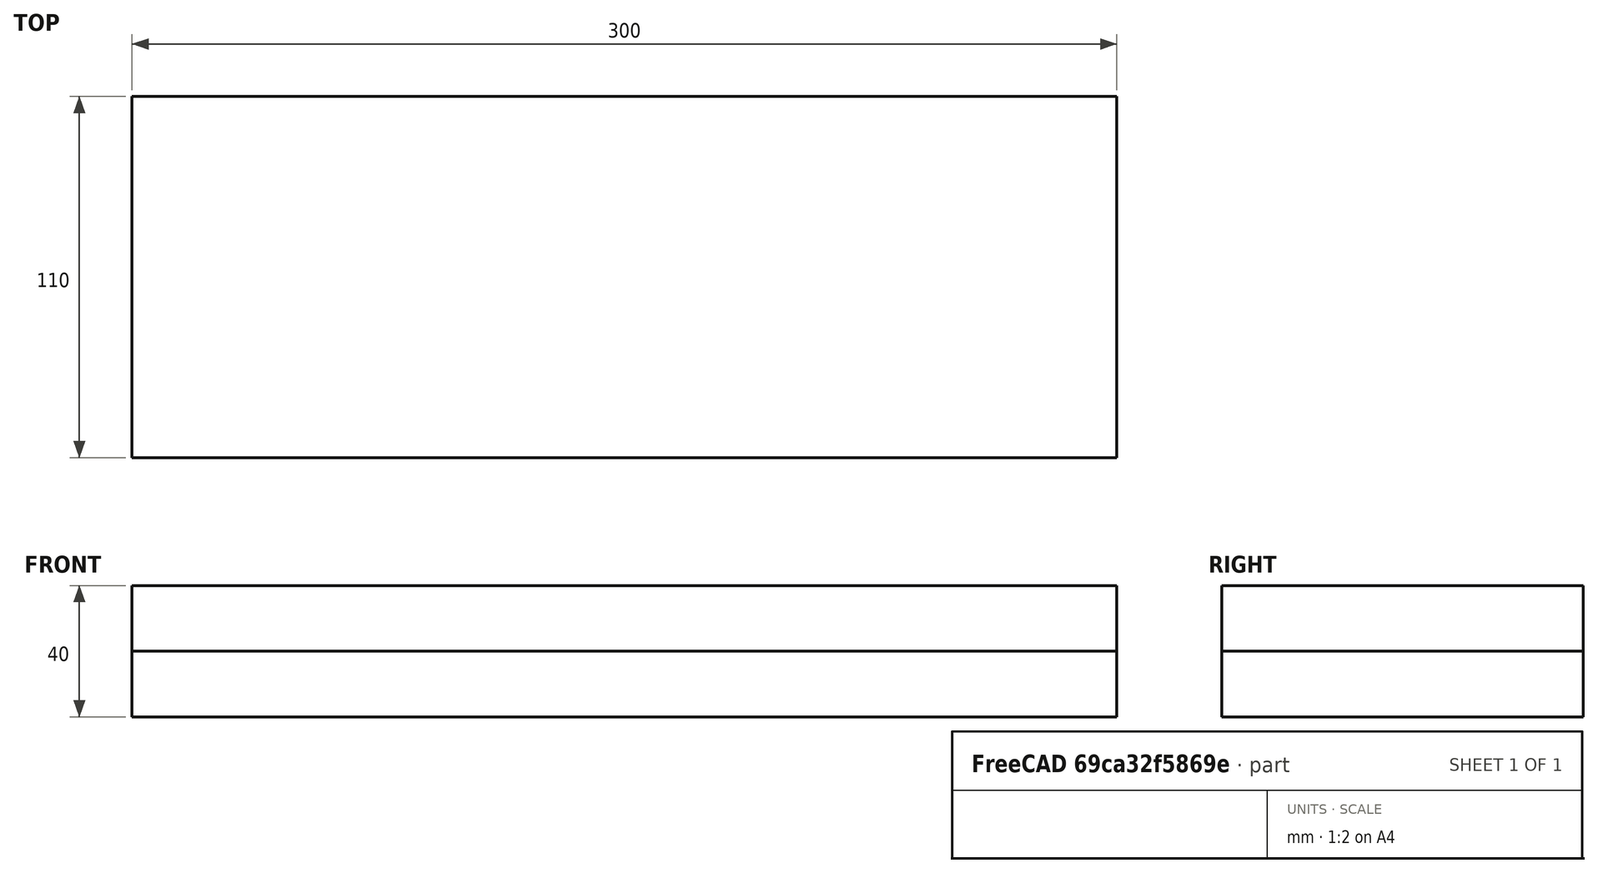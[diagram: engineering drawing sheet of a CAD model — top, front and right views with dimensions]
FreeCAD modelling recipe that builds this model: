
FCSTD DOCUMENT  (FreeCAD 0.19R24276 (Git))
Label: case
License: All rights reserved
LicenseURL: http://en.wikipedia.org/wiki/All_rights_reserved
objects: Sketcher::SketchObject×4, Part::FeaturePython×3, PartDesign::Pad×1, Part::Plane×1, PartDesign::Body×1, App::DocumentObjectGroup×1, PartDesign::ShapeBinder×1
note: 12 computed .brp shape members not serialized (recipe doc carries the construction recipe); baked Part::Feature solids carry a one-line shape summary decoded from their .brp

FEATURE [Sketcher::SketchObject] Sketch
  FullyConstrained = true
  MapMode = 5
  Support = -> [XY_Plane]
  sketch-geometry (4):
    g0: LineSegment StartX=-150 StartY=55 StartZ=0 EndX=150 EndY=55 EndZ=0
    g1: LineSegment StartX=150 StartY=55 StartZ=0 EndX=150 EndY=-55 EndZ=0
    g2: LineSegment StartX=150 StartY=-55 StartZ=0 EndX=-150 EndY=-55 EndZ=0
    g3: LineSegment StartX=-150 StartY=-55 StartZ=0 EndX=-150 EndY=55 EndZ=0
  constraints (10):
    c: Coincident(g0,g1)
    c: Coincident(g1,g2)
    c: Coincident(g2,g3)
    c: Coincident(g3,g0)
    c: Horizontal(g2)
    c: Vertical(g1)
    c: DistanceX(g0,g0) = 300
    c: DistanceY(g1,g1) = 110
    c: Symmetric(g0,g2,g-1)
    c: Symmetric(g0,g0,g-2)
FEATURE [PartDesign::Pad] Pad
  Direction = (1,1,1)
  Length = 40
  Length2 = 100
  Profile = -> Sketch
  Type = 0
FEATURE [Part::Plane] Plane
  AttacherType = Attacher::AttachEngine3D
  Length = 500
  Placement = pos=(-226,-161,20) rot=(0,0,1;0rad)
  Width = 500
FEATURE [PartDesign::Body] Body
  Group = -> [Sketch,Pad,CopySlice_child1,Sketch001]
  Origin = -> Origin
  Tip = -> Pad
FEATURE [Part::FeaturePython] Slice  # WARN: FeaturePython — macro-defined, semantics opaque (R4)
  Base = -> Body
  Mode = 1
  Tolerance = 0
  Tools = -> [Plane]
FEATURE [App::DocumentObjectGroup] GrExplode_Slice  label="Exploded Slice"
  Group = -> [Slice_child0,Slice_child1,Sketch002,Sketch003]
FEATURE [Part::FeaturePython] Slice_child0  label="Slice.0"  # WARN: FeaturePython — macro-defined, semantics opaque (R4)
  Base = -> Slice
  FilterType = 1
  Invert = false
  OverrideMaxVal = 0
  WindowFrom = 80
  WindowTo = 100
  items = 0
FEATURE [Part::FeaturePython] Slice_child1  label="Slice.1"  # WARN: FeaturePython — macro-defined, semantics opaque (R4)
  Base = -> Slice
  FilterType = 1
  Invert = false
  OverrideMaxVal = 0
  WindowFrom = 80
  WindowTo = 100
  items = 1
FEATURE [PartDesign::ShapeBinder] CopySlice_child1
  Support = -> [Slice_child0]
  TraceSupport = false
FEATURE [Sketcher::SketchObject] Sketch001
  FullyConstrained = true
  MapMode = 5
  Placement = pos=(0,0,20) rot=(0,0,1;0rad)
  Support = -> [CopySlice_child1]
FEATURE [Sketcher::SketchObject] Sketch003
  FullyConstrained = true
  MapMode = 5
  Placement = pos=(0,0,40) rot=(0,0,1;0rad)
  Support = -> [Slice_child1]
  sketch-geometry (4):
    g0: LineSegment StartX=-141.25 StartY=46.25 StartZ=0 EndX=141.25 EndY=46.25 EndZ=0
    g1: LineSegment StartX=141.25 StartY=46.25 StartZ=0 EndX=141.25 EndY=-46.25 EndZ=0
    g2: LineSegment StartX=141.25 StartY=-46.25 StartZ=0 EndX=-141.25 EndY=-46.25 EndZ=0
    g3: LineSegment StartX=-141.25 StartY=-46.25 StartZ=0 EndX=-141.25 EndY=46.25 EndZ=0
  constraints (10):
    c: Coincident(g0,g1)
    c: Coincident(g1,g2)
    c: Coincident(g2,g3)
    c: Coincident(g3,g0)
    c: Horizontal(g2)
    c: Vertical(g1)
    c: Symmetric(g0,g0,g-2)
    c: Symmetric(g0,g2,g-1)
    c: DistanceX(g0,g0) = 282.5
    c: DistanceY(g1,g1) = 92.5
FEATURE [Sketcher::SketchObject] Sketch002
  FullyConstrained = true
  MapMode = 2
  Support = -> [Slice_child1]
